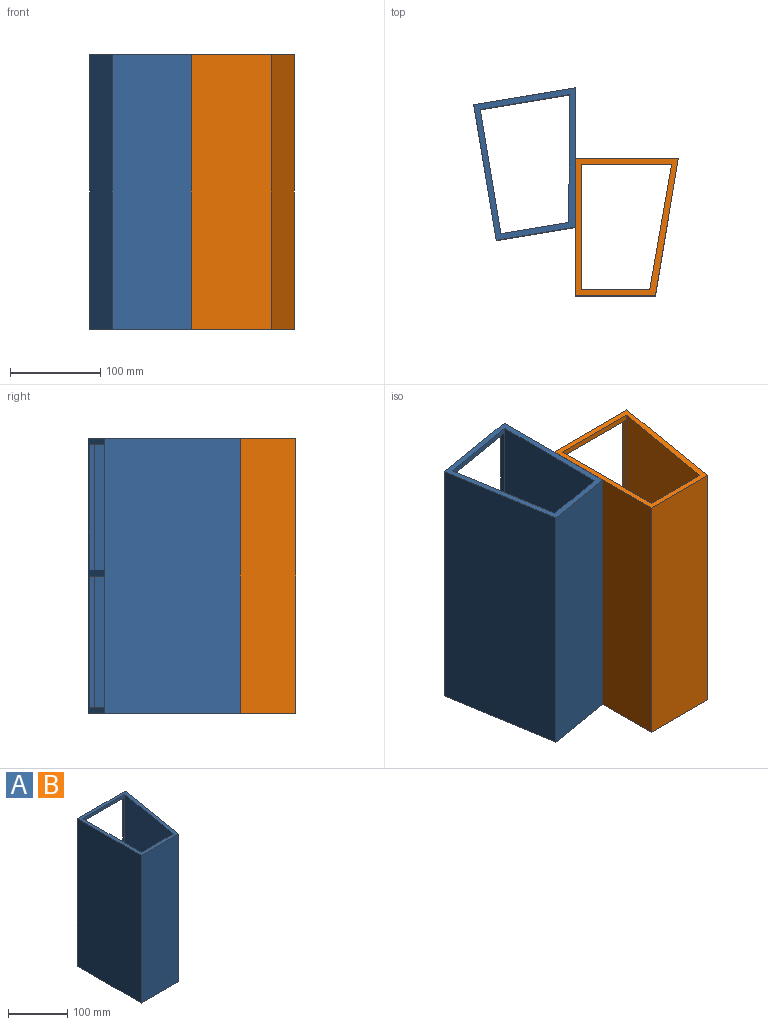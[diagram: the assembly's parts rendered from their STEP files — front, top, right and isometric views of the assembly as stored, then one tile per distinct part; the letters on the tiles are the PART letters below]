
ASSEMBLY  parts=2 mates=1
PART A: 16 faces, bbox 114.3x152.4x304.8 mm
  f0: plane 304.8x100.54mm, normal (0,-1,0), area 1940.3mm2, adj f3,f7,f8,f9,f10,f11,f12,f13
  f1: plane 304.8x114.3mm, normal (0,1,0), area 5831.5mm2, adj f3,f5,f6,f8,f9,f10,f11,f12
  f2: plane 304.8x76.2mm, normal (0,1,0), area 23225.8mm2, adj f3,f7,f8,f12
  f3: plane 304.8x146.05mm, normal (1,0,0), area 44395.1mm2, adj f0,f1,f2,f8,f10,f11,f12,f14
  f4: plane 304.8x88.9mm, normal (0,-1,0), area 27096.7mm2, adj f5,f6,f8,f12
  f5: plane 304.8x152.4mm, normal (0.99,-0.16,0), area 47092.3mm2, adj f1,f4,f8,f12
  f6: plane 304.8x152.4mm, normal (-1,0,0), area 46451.5mm2, adj f1,f4,f8,f12
  f7: plane 304.8x139.7mm, normal (-0.99,0.17,0), area 43222.1mm2, adj f0,f2,f8,f12
  f8: plane 152.4x114.3mm, normal (0,0,1), area 3138.4mm2, adj f0,f1,f2,f3,f4,f5,f6,f7
  f9: plane 139.7x6.35mm, normal (-0.99,0.16,0), area 899.3mm2, adj f0,f1,f10,f11
  f10: plane 101.51x6.35mm, normal (0,0,-1), area 641.2mm2, adj f0,f1,f3,f9
  f11: plane 101.51x6.35mm, normal (0,0,1), area 641.2mm2, adj f0,f1,f3,f9
  f12: plane 152.4x114.3mm, normal (0,0,-1), area 3138.4mm2, adj f0,f1,f2,f3,f4,f5,f6,f7
  f13: plane 146.05x6.35mm, normal (-0.99,0.16,0), area 940.2mm2, adj f0,f1,f14,f15
  f14: plane 101.51x6.35mm, normal (0,0,-1), area 641.2mm2, adj f0,f1,f3,f13
  f15: plane 101.51x6.35mm, normal (0,0,1), area 641.2mm2, adj f0,f1,f3,f13
PART B: same geometry as A
PLACE A rot(axis=(0,0,1),9.5deg) t=(-56.61,87.08,18.04)mm
PLACE B t=(44.21,19.22,18.04)mm
MATE parallel A.f5 <-> B.f6  axis (1,0,0) through (-0.24,19.22,-134.36)mm
